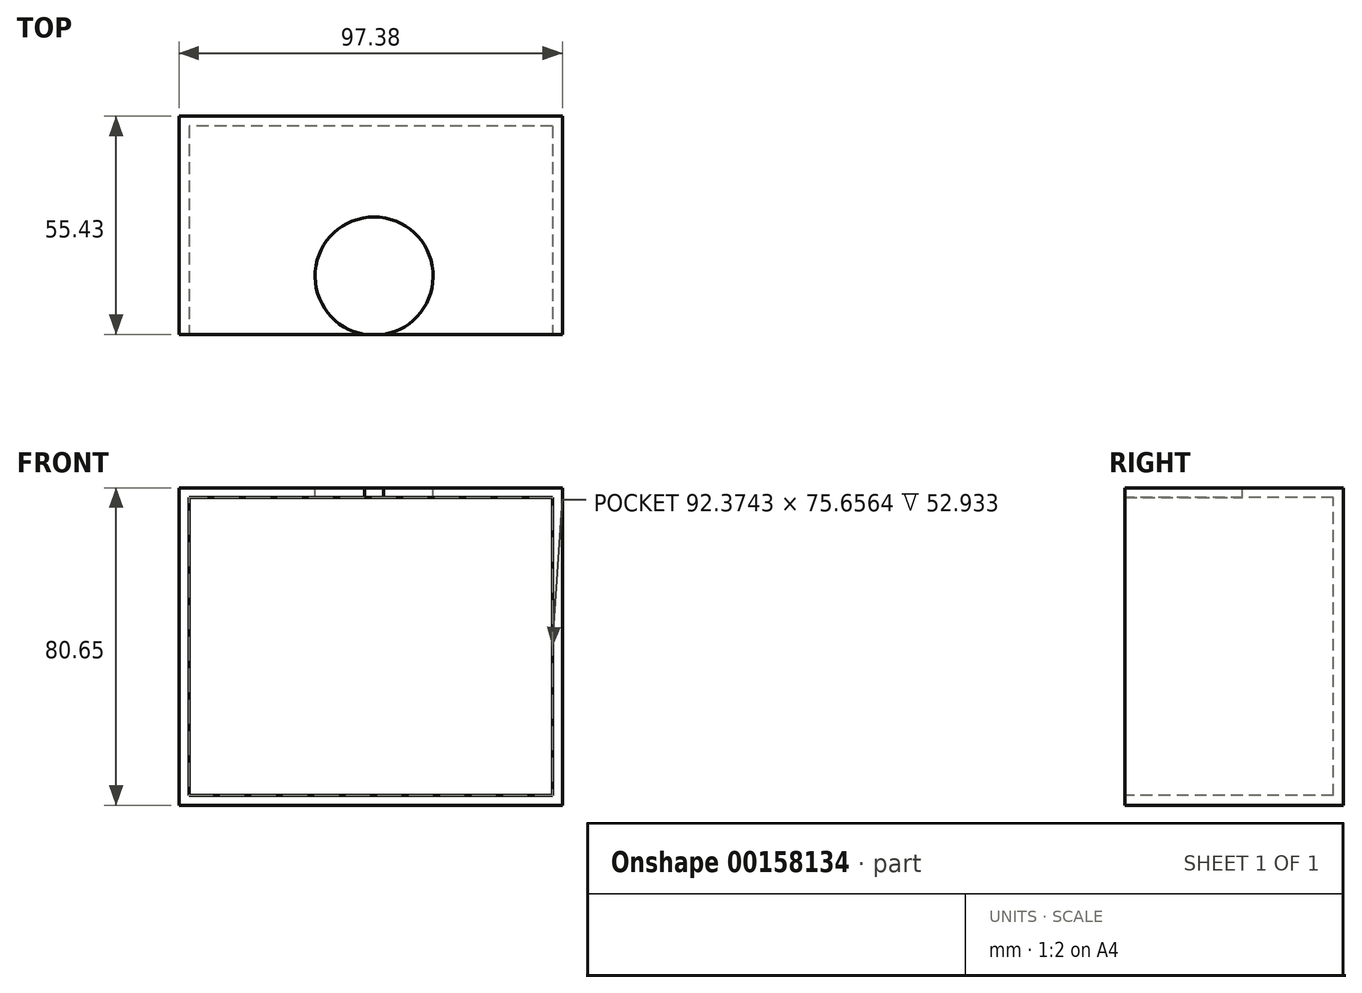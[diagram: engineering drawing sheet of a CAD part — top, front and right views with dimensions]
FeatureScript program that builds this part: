
annotation { "Feature Type Name" : "Feature", "Feature Type Description" : "" }
export const myFeature = defineFeature(function(context is Context, id is Id, definition is map)
    precondition{}
    {
        {
            var Q0;
            Q0=qCreatedBy(makeId("Front.planeOp"),FACE);
            var sketch = newSketch(context, id + "F0", { "sketchPlane" : qUnion([Q0])});
            skLineSegment(sketch, "E0", {"start": v(-49.57, 42.09) * mm, "end": v(-49.57, -32.7) * mm});
            skLineSegment(sketch, "E1", {"start": v(-49.57, -32.7) * mm, "end": v(47.8, -32.7) * mm});
            skLineSegment(sketch, "E2", {"start": v(47.8, -32.7) * mm, "end": v(47.8, 47.95) * mm});
            skLineSegment(sketch, "E3", {"start": v(47.8, 47.95) * mm, "end": v(-49.57, 47.95) * mm});
            skLineSegment(sketch, "E4", {"start": v(-49.57, 47.95) * mm, "end": v(-49.57, 42.09) * mm});
            skSolve(sketch);
        }
        {
            var Q0;
            Q0=qCreatedBy(makeId("Right.planeOp"),FACE);
            var sketch = newSketch(context, id + "F1", { "sketchPlane" : qUnion([Q0])});
            skLineSegment(sketch, "E5", {"start": v(0, 0) * mm, "end": v(-55.43, 0) * mm});
            skSolve(sketch);
        }
        {
            var Q0;
            Q0=makeQuery(id+"F0.imprint","IMPRINT",FACE,{"disambiguationData":[TD([[makeQuery(id+"F0.imprint","IMPRINT",EDGE,{"derivedFrom":sQuery(id+"F0.wireOp",EDGE,"E0")}),1.0]])]});
            var Q1;
            Q1=sQuery(id+"F1.wireOp",EDGE,"E5");
            sweep(context, id + "F2", {"profiles" : qUnion([Q0]), "path" : qUnion([Q1])});
        }
        {
            var Q0;
            Q0=makeQuery(id+"F2.opSweep","CAP_FACE",FACE,{"disambiguationData":[OSD([sQuery(id+"F0.wireOp",EDGE,"E0"),sQuery(id+"F0.wireOp",EDGE,"E1"),sQuery(id+"F0.wireOp",EDGE,"E2"),sQuery(id+"F0.wireOp",EDGE,"E3"),sQuery(id+"F0.wireOp",EDGE,"E4"),sQuery(id+"F1.wireOp",VERTEX,"E5.end")])],"isStart":false});
            shell(context, id + "F3", {"entities" : qUnion([Q0]), "thickness" : 2.5 * mm});
        }
        {
            var Q0;
            Q0=makeQuery(id+"F2.opSweep","SWEPT_FACE",FACE,{"disambiguationData":[OSD([sQuery(id+"F0.wireOp",EDGE,"E3"),sQuery(id+"F1.wireOp",EDGE,"E5")])]});
            var sketch = newSketch(context, id + "F4", { "sketchPlane" : qUnion([Q0])});
            skPoint(sketch, "E6", {"position": v(0, -40.62) * mm});
            skSolve(sketch);
        }
        {
            var Q0;
            Q0=sQuery(id+"F4.wireOp",VERTEX,"E6");
            var Q1;
            Q1=makeQuery(id+"F2.opSweep","SWEPT_BODY",BODY,{"disambiguationData":[OSD([sQuery(id+"F0.wireOp",EDGE,"E0"),sQuery(id+"F0.wireOp",EDGE,"E1"),sQuery(id+"F0.wireOp",EDGE,"E2"),sQuery(id+"F0.wireOp",EDGE,"E3"),sQuery(id+"F0.wireOp",EDGE,"E4"),sQuery(id+"F1.wireOp",EDGE,"E5")])]});
            hole(context, id + "F5", {"style" : HoleStyle.SIMPLE, "endStyle" : HoleEndStyle.BLIND, "holeDiameter" : 30 * mm, "holeDepth" : 12 * mm, "locations" : qUnion([Q0]), "scope" : qUnion([Q1])});
        }
    });
